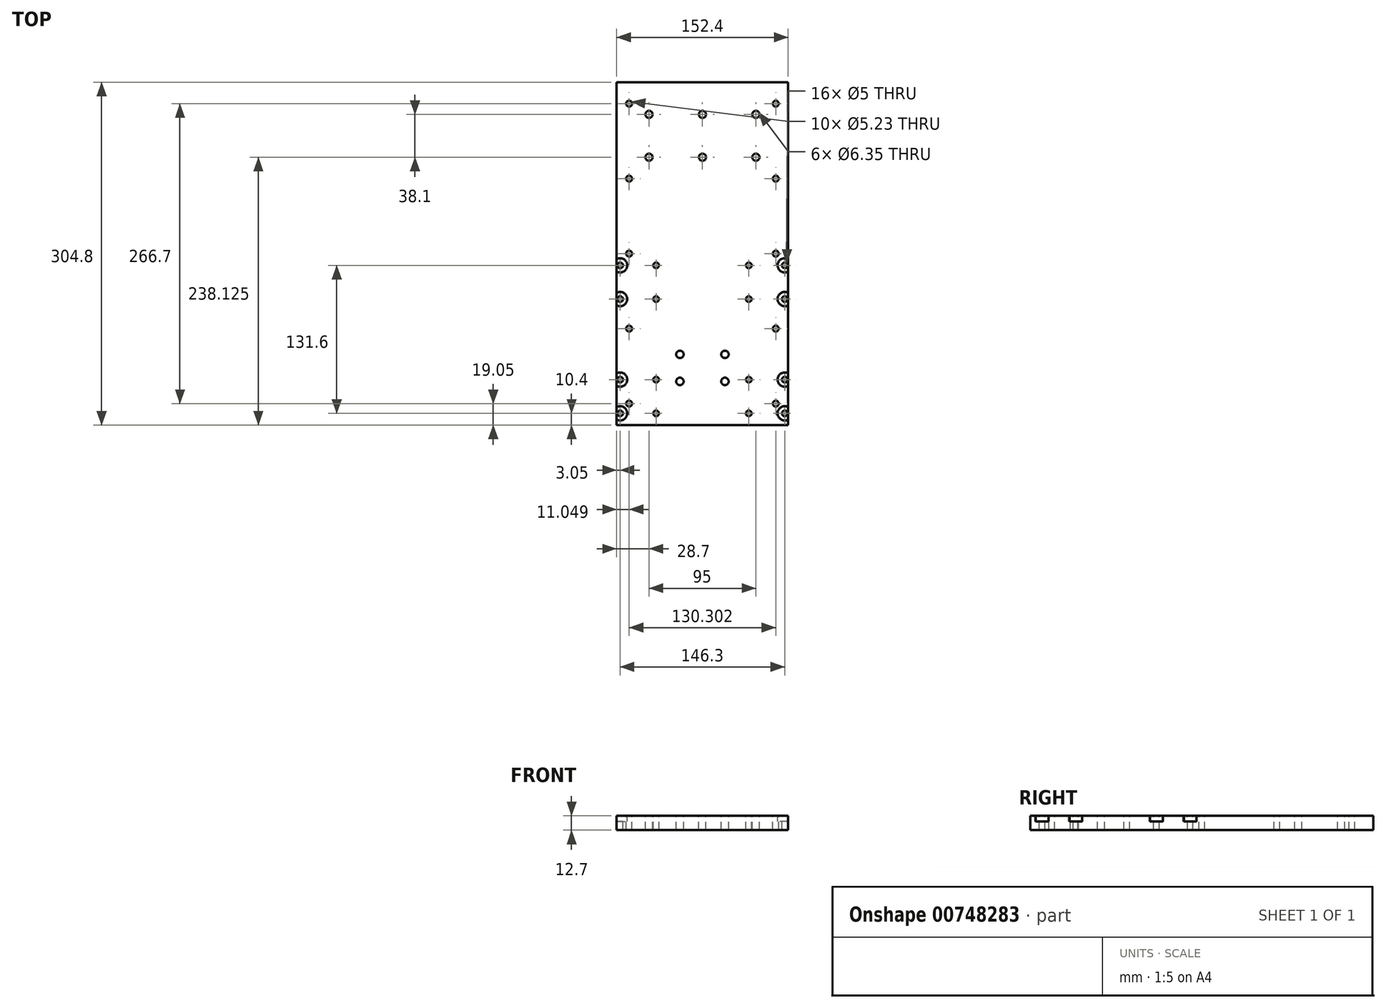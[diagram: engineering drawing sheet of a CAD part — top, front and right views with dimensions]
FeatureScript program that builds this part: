
annotation { "Feature Type Name" : "Feature", "Feature Type Description" : "" }
export const myFeature = defineFeature(function(context is Context, id is Id, definition is map)
    precondition{}
    {
        {
            var Q0;
            Q0=qCreatedBy(makeId("Front.planeOp"),FACE);
            var sketch = newSketch(context, id + "F0", { "sketchPlane" : qUnion([Q0])});
            skLineSegment(sketch, "E0.bottom", {"start": v(76.2, 6.35) * mm, "end": v(-76.2, 6.35) * mm});
            skLineSegment(sketch, "E0.top", {"start": v(76.2, -6.35) * mm, "end": v(-76.2, -6.35) * mm});
            skLineSegment(sketch, "E0.left", {"start": v(76.2, 6.35) * mm, "end": v(76.2, -6.35) * mm});
            skLineSegment(sketch, "E0.right", {"start": v(-76.2, 6.35) * mm, "end": v(-76.2, -6.35) * mm});
            skPoint(sketch, "E0.middle", {"position": v(0, 0) * mm});
            skSolve(sketch);
        }
        {
            var Q0;
            Q0 = qSketchRegion(id + "F0", true);
            extrude(context, id + "F1", {"entities" : qUnion([Q0]), "depth" : 304.8 * mm, "offsetDistance" : 25.4 * mm});
        }
        {
            var Q0;
            Q0=makeQuery(id+"F1.opExtrude","SWEPT_FACE",FACE,{"disambiguationData":[OSD([sQuery(id+"F0.wireOp",EDGE,"E0.bottom")])]});
            var sketch = newSketch(context, id + "F2", { "sketchPlane" : qUnion([Q0])});
            skLineSegment(sketch, "E1", {"start": v(0, 0) * mm, "end": v(0, -304.8) * mm, "construction": true});
            skLineSegment(sketch, "E2", {"start": v(-76.2, -254) * mm, "end": v(76.2, -254) * mm, "construction": true});
            skLineSegment(sketch, "E3.0", {"start": v(57.15, 0) * mm, "end": v(57.15, -330.2) * mm, "construction": true});
            skLineSegment(sketch, "E4.0", {"start": v(-57.15, 0) * mm, "end": v(-57.15, -330.2) * mm, "construction": true});
            skLineSegment(sketch, "E5.0", {"start": v(-76.2, -279.4) * mm, "end": v(76.2, -279.4) * mm, "construction": true});
            skLineSegment(sketch, "E6.0", {"start": v(-76.2, -177.8) * mm, "end": v(76.2, -177.8) * mm, "construction": true});
            skLineSegment(sketch, "E7.bottom", {"start": v(-41.15, -264.4) * mm, "end": v(-73.15, -264.4) * mm, "construction": true});
            skLineSegment(sketch, "E7.top", {"start": v(-41.15, -294.4) * mm, "end": v(-73.15, -294.4) * mm, "construction": true});
            skLineSegment(sketch, "E7.left", {"start": v(-41.15, -264.4) * mm, "end": v(-41.15, -294.4) * mm, "construction": true});
            skLineSegment(sketch, "E7.right", {"start": v(-73.15, -264.4) * mm, "end": v(-73.15, -294.4) * mm, "construction": true});
            skPoint(sketch, "E7.middle", {"position": v(-57.15, -279.4) * mm});
            skLineSegment(sketch, "E8.bottom", {"start": v(-41.15, -162.8) * mm, "end": v(-73.15, -162.8) * mm, "construction": true});
            skLineSegment(sketch, "E8.top", {"start": v(-41.15, -192.8) * mm, "end": v(-73.15, -192.8) * mm, "construction": true});
            skLineSegment(sketch, "E8.left", {"start": v(-41.15, -162.8) * mm, "end": v(-41.15, -192.8) * mm, "construction": true});
            skLineSegment(sketch, "E8.right", {"start": v(-73.15, -162.8) * mm, "end": v(-73.15, -192.8) * mm, "construction": true});
            skPoint(sketch, "E8.middle", {"position": v(-57.15, -177.8) * mm});
            skLineSegment(sketch, "E9.bottom", {"start": v(41.15, -162.8) * mm, "end": v(73.15, -162.8) * mm, "construction": true});
            skLineSegment(sketch, "E9.top", {"start": v(41.15, -192.8) * mm, "end": v(73.15, -192.8) * mm, "construction": true});
            skLineSegment(sketch, "E9.left", {"start": v(41.15, -162.8) * mm, "end": v(41.15, -192.8) * mm, "construction": true});
            skLineSegment(sketch, "E9.right", {"start": v(73.15, -162.8) * mm, "end": v(73.15, -192.8) * mm, "construction": true});
            skPoint(sketch, "E9.middle", {"position": v(57.15, -177.8) * mm});
            skLineSegment(sketch, "E10.bottom", {"start": v(73.15, -264.4) * mm, "end": v(41.15, -264.4) * mm, "construction": true});
            skLineSegment(sketch, "E10.top", {"start": v(73.15, -294.4) * mm, "end": v(41.15, -294.4) * mm, "construction": true});
            skLineSegment(sketch, "E10.left", {"start": v(73.15, -264.4) * mm, "end": v(73.15, -294.4) * mm, "construction": true});
            skLineSegment(sketch, "E10.right", {"start": v(41.15, -264.4) * mm, "end": v(41.15, -294.4) * mm, "construction": true});
            skPoint(sketch, "E10.middle", {"position": v(57.15, -279.4) * mm});
            skCircle(sketch, "E11", {"center": v(-73.15, -294.4) * mm, "radius": 2.5 * mm});
            skCircle(sketch, "E12", {"center": v(-41.15, -294.4) * mm, "radius": 2.5 * mm});
            skCircle(sketch, "E13", {"center": v(-73.15, -264.4) * mm, "radius": 2.5 * mm});
            skCircle(sketch, "E14", {"center": v(-41.15, -264.4) * mm, "radius": 2.5 * mm});
            skCircle(sketch, "E15", {"center": v(-73.15, -162.8) * mm, "radius": 2.5 * mm});
            skCircle(sketch, "E16", {"center": v(-73.15, -192.8) * mm, "radius": 2.5 * mm});
            skCircle(sketch, "E17", {"center": v(-41.15, -192.8) * mm, "radius": 2.5 * mm});
            skCircle(sketch, "E18", {"center": v(-41.15, -162.8) * mm, "radius": 2.5 * mm});
            skCircle(sketch, "E19", {"center": v(41.15, -162.8) * mm, "radius": 2.5 * mm});
            skCircle(sketch, "E20", {"center": v(41.15, -192.8) * mm, "radius": 2.5 * mm});
            skCircle(sketch, "E21", {"center": v(73.15, -162.8) * mm, "radius": 2.5 * mm});
            skCircle(sketch, "E22", {"center": v(73.15, -192.8) * mm, "radius": 2.5 * mm});
            skCircle(sketch, "E23", {"center": v(41.15, -264.4) * mm, "radius": 2.5 * mm});
            skCircle(sketch, "E24", {"center": v(73.15, -264.4) * mm, "radius": 2.5 * mm});
            skCircle(sketch, "E25", {"center": v(41.15, -294.4) * mm, "radius": 2.5 * mm});
            skCircle(sketch, "E26", {"center": v(73.15, -294.4) * mm, "radius": 2.5 * mm});
            skLineSegment(sketch, "E27.bottom", {"start": v(20, -242) * mm, "end": v(-20, -242) * mm, "construction": true});
            skLineSegment(sketch, "E27.top", {"start": v(20, -266) * mm, "end": v(-20, -266) * mm, "construction": true});
            skLineSegment(sketch, "E27.left", {"start": v(20, -242) * mm, "end": v(20, -266) * mm, "construction": true});
            skLineSegment(sketch, "E27.right", {"start": v(-20, -242) * mm, "end": v(-20, -266) * mm, "construction": true});
            skPoint(sketch, "E27.middle", {"position": v(0, -254) * mm});
            skCircle(sketch, "E28", {"center": v(-20, -266) * mm, "radius": 3.3 * mm});
            skCircle(sketch, "E29", {"center": v(-20, -242) * mm, "radius": 3.3 * mm});
            skCircle(sketch, "E30", {"center": v(20, -242) * mm, "radius": 3.3 * mm});
            skCircle(sketch, "E31", {"center": v(20, -266) * mm, "radius": 3.3 * mm});
            skLineSegment(sketch, "E32.bottom", {"start": v(47.5, -66.68) * mm, "end": v(-47.5, -66.68) * mm, "construction": true});
            skLineSegment(sketch, "E32.top", {"start": v(47.5, -28.58) * mm, "end": v(-47.5, -28.58) * mm, "construction": true});
            skLineSegment(sketch, "E32.left", {"start": v(47.5, -66.68) * mm, "end": v(47.5, -28.58) * mm, "construction": true});
            skLineSegment(sketch, "E32.right", {"start": v(-47.5, -66.68) * mm, "end": v(-47.5, -28.58) * mm, "construction": true});
            skPoint(sketch, "E32.middle", {"position": v(0, -47.63) * mm});
            skCircle(sketch, "E33", {"center": v(47.5, -28.58) * mm, "radius": 3.18 * mm});
            skCircle(sketch, "E34", {"center": v(0, -28.58) * mm, "radius": 3.18 * mm});
            skCircle(sketch, "E35", {"center": v(-47.5, -28.58) * mm, "radius": 3.18 * mm});
            skCircle(sketch, "E36", {"center": v(-47.5, -66.68) * mm, "radius": 3.18 * mm});
            skCircle(sketch, "E37", {"center": v(0, -66.68) * mm, "radius": 3.18 * mm});
            skCircle(sketch, "E38", {"center": v(47.5, -66.68) * mm, "radius": 3.18 * mm});
            skLineSegment(sketch, "E39", {"start": v(65.15, 0) * mm, "end": v(65.15, -304.8) * mm, "construction": true});
            skLineSegment(sketch, "E40", {"start": v(-65.15, 0) * mm, "end": v(-65.15, -304.8) * mm, "construction": true});
            skCircle(sketch, "E41", {"center": v(65.15, -19.05) * mm, "radius": 2.62 * mm});
            skCircle(sketch, "E42", {"center": v(65.15, -85.73) * mm, "radius": 2.62 * mm});
            skCircle(sketch, "E43", {"center": v(65.15, -152.4) * mm, "radius": 2.62 * mm});
            skCircle(sketch, "E44", {"center": v(65.15, -219.08) * mm, "radius": 2.62 * mm});
            skCircle(sketch, "E45", {"center": v(65.15, -285.75) * mm, "radius": 2.62 * mm});
            skCircle(sketch, "E46", {"center": v(-65.15, -19.05) * mm, "radius": 2.62 * mm});
            skCircle(sketch, "E47", {"center": v(-65.15, -85.73) * mm, "radius": 2.62 * mm});
            skCircle(sketch, "E48", {"center": v(-65.15, -152.4) * mm, "radius": 2.62 * mm});
            skCircle(sketch, "E49", {"center": v(-65.15, -219.08) * mm, "radius": 2.62 * mm});
            skCircle(sketch, "E50", {"center": v(-65.15, -285.75) * mm, "radius": 2.62 * mm});
            skSolve(sketch);
        }
        {
            var Q0;
            Q0 = qSketchRegion(id + "F2", true);
            extrude(context, id + "F3", {"entities" : qUnion([Q0]), "operationType" : NewBodyOperationType.REMOVE, "endBound" : BoundingType.THROUGH_ALL, "oppositeDirection" : true, "depth" : 25.4 * mm, "offsetDistance" : 25.4 * mm});
        }
        {
            var Q0;
            Q0=makeQuery(id+"F1.opExtrude","SWEPT_FACE",FACE,{"disambiguationData":[OSD([sQuery(id+"F0.wireOp",EDGE,"E0.bottom")])]});
            var sketch = newSketch(context, id + "F4", { "sketchPlane" : qUnion([Q0])});
            skCircle(sketch, "E51", {"center": v(-73.15, -294.4) * mm, "radius": 6.35 * mm});
            skCircle(sketch, "E52", {"center": v(-73.15, -264.4) * mm, "radius": 6.35 * mm});
            skCircle(sketch, "E53", {"center": v(-73.15, -192.8) * mm, "radius": 6.35 * mm});
            skCircle(sketch, "E54", {"center": v(-73.15, -162.8) * mm, "radius": 6.35 * mm});
            skCircle(sketch, "E55", {"center": v(73.15, -162.8) * mm, "radius": 6.35 * mm});
            skCircle(sketch, "E56", {"center": v(73.15, -192.8) * mm, "radius": 6.35 * mm});
            skCircle(sketch, "E57", {"center": v(73.15, -264.4) * mm, "radius": 6.35 * mm});
            skCircle(sketch, "E58", {"center": v(73.15, -294.4) * mm, "radius": 6.35 * mm});
            skSolve(sketch);
        }
        {
            var Q0;
            Q0 = qSketchRegion(id + "F4", true);
            extrude(context, id + "F5", {"entities" : qUnion([Q0]), "operationType" : NewBodyOperationType.REMOVE, "oppositeDirection" : true, "depth" : 5.08 * mm, "offsetDistance" : 25.4 * mm});
        }
    });
